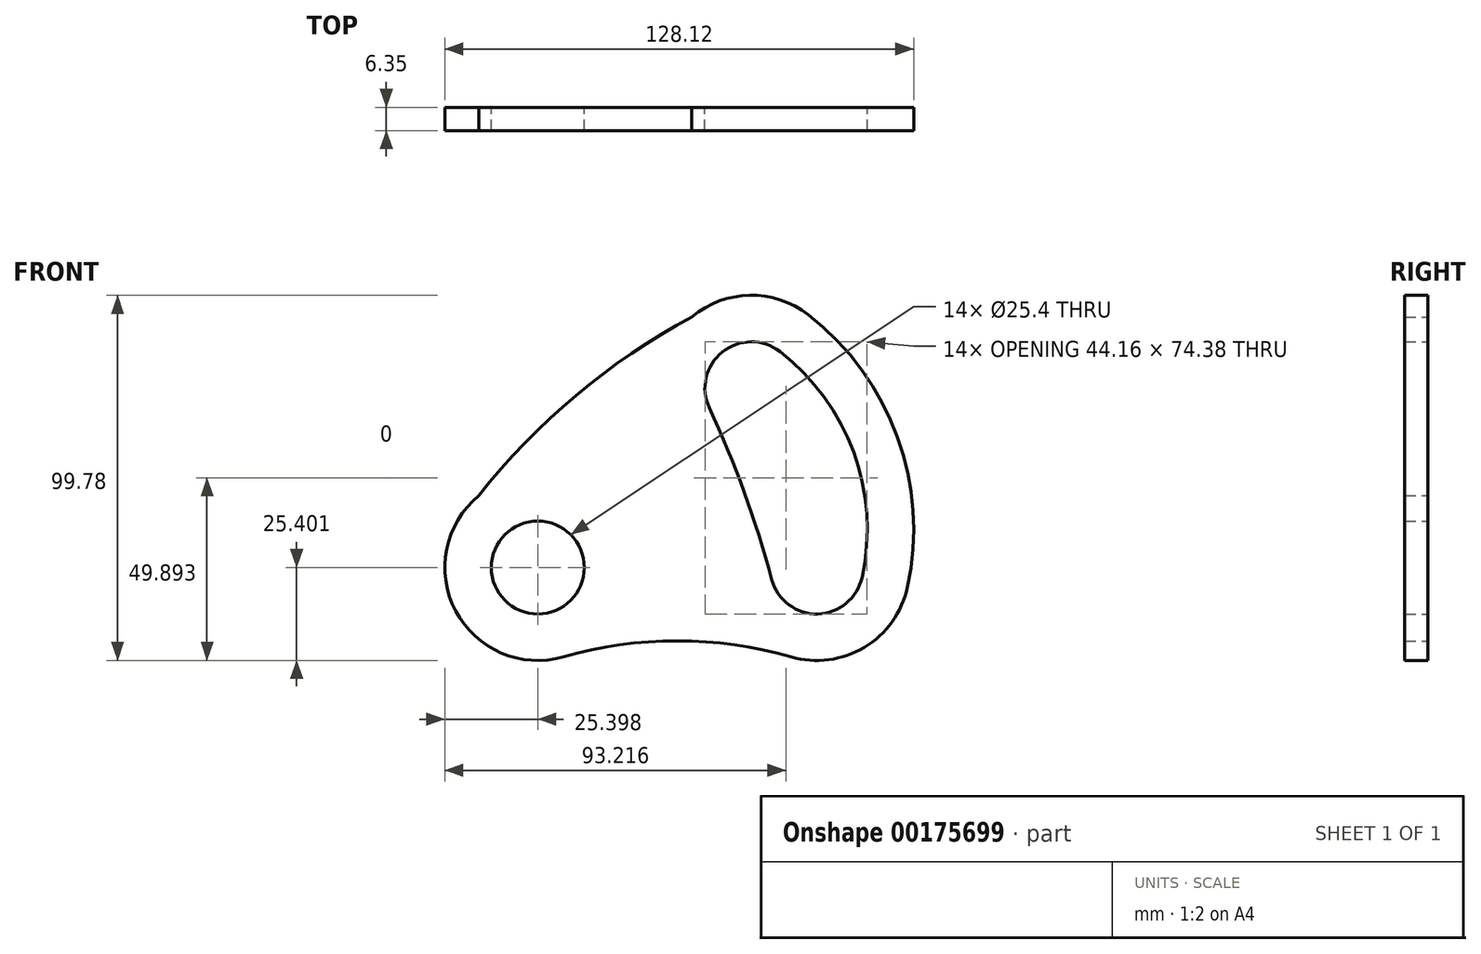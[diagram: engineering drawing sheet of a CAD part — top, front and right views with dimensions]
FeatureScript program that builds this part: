
annotation { "Feature Type Name" : "Feature", "Feature Type Description" : "" }
export const myFeature = defineFeature(function(context is Context, id is Id, definition is map)
    precondition{}
    {
        {
            var Q0;
            Q0=qCreatedBy(makeId("Front.planeOp"),FACE);
            var sketch = newSketch(context, id + "F0", { "sketchPlane" : qUnion([Q0])});
            skCircle(sketch, "E0", {"center": v(-42.07, 4.01) * mm, "radius": 25.4 * mm});
            skCircle(sketch, "E1", {"center": v(-42.07, 4.01) * mm, "radius": 12.7 * mm});
            skCircle(sketch, "E2", {"center": v(16.3, 53) * mm, "radius": 12.7 * mm});
            skCircle(sketch, "E3", {"center": v(34.13, 4.01) * mm, "radius": 12.7 * mm});
            skLineSegment(sketch, "E4", {"start": v(-42.07, 4.01) * mm, "end": v(34.13, 4.01) * mm});
            skLineSegment(sketch, "E5", {"start": v(-42.07, 4.01) * mm, "end": v(16.3, 53) * mm});
            skArc(sketch, "E6", {"start": v(21.86, 0.72) * mm, "mid": v(14.35, 24.55) * mm, "end": v(4.79, 47.63) * mm});
            skArc(sketch, "E7", {"start": v(46.53, 1.29) * mm, "mid": v(44.26, 35.43) * mm, "end": v(24.05, 63.05) * mm});
            skCircle(sketch, "E8", {"center": v(16.3, 53) * mm, "radius": 25.4 * mm});
            skCircle(sketch, "E9", {"center": v(34.13, 4.01) * mm, "radius": 25.4 * mm});
            skArc(sketch, "E10", {"start": v(58.95, -1.4) * mm, "mid": v(56.18, 39.77) * mm, "end": v(31.83, 73.09) * mm});
            skArc(sketch, "E11", {"start": v(8.74, 4.9) * mm, "mid": v(6.11, 21.55) * mm, "end": v(-2.57, 35.99) * mm});
            skArc(sketch, "E12", {"start": v(0, 72.47) * mm, "mid": v(-31.62, 51.02) * mm, "end": v(-58.23, 23.6) * mm});
            skArc(sketch, "E13", {"start": v(27.13, -20.4) * mm, "mid": v(-3.97, -16.04) * mm, "end": v(-35.07, -20.4) * mm});
            skSolve(sketch);
        }
        {
            var Q0;
            {var subQ0=sQuery(id+"F0.wireOp",EDGE,"E12");Q0=makeQuery(id+"F0.imprint","IMPRINT",FACE,{"disambiguationData":[TD([[makeQuery(id+"F0.imprint","IMPRINT",EDGE,{"derivedFrom":subQ0}),1.0]])]});}
            var Q1;
            {var subQ9=sQuery(id+"F0.wireOp",EDGE,"E11");Q1=makeQuery(id+"F0.imprint","IMPRINT",FACE,{"disambiguationData":[TD([[makeQuery(id+"F0.imprint","IMPRINT",EDGE,{"derivedFrom":subQ9}),1.0]])]});}
            var Q2;
            {var subQ0=sQuery(id+"F0.wireOp",EDGE,"E13");Q2=makeQuery(id+"F0.imprint","IMPRINT",FACE,{"disambiguationData":[TD([[makeQuery(id+"F0.imprint","IMPRINT",EDGE,{"derivedFrom":subQ0}),-1.0]])]});}
            var Q3;
            {var subQ5=sQuery(id+"F0.wireOp",EDGE,"E10");Q3=makeQuery(id+"F0.imprint","IMPRINT",FACE,{"disambiguationData":[TD([[makeQuery(id+"F0.imprint","IMPRINT",EDGE,{"derivedFrom":subQ5}),1.0]])]});}
            var Q4;
            {var subQ1=sQuery(id+"F0.wireOp",EDGE,"E2");var subQ5=sQuery(id+"F0.wireOp",EDGE,"E6");var subQ6=makeQuery(id+"F0.imprint","INTERSECT",VERTEX,{"derivedFrom":[subQ1,subQ5]});Q4=makeQuery(id+"F0.imprint","IMPRINT",FACE,{"disambiguationData":[TD([[makeQuery(id+"F0.imprint","IMPRINT",EDGE,{"disambiguationData":[TD([[subQ6,1.0]])],"derivedFrom":subQ1}),-1.0]])]});}
            var Q5;
            {var subQ0=sQuery(id+"F0.wireOp",EDGE,"E6");var subQ1=sQuery(id+"F0.wireOp",EDGE,"E3");var subQ2=makeQuery(id+"F0.imprint","INTERSECT",VERTEX,{"derivedFrom":[subQ1,subQ0]});Q5=makeQuery(id+"F0.imprint","IMPRINT",FACE,{"disambiguationData":[TD([[makeQuery(id+"F0.imprint","IMPRINT",EDGE,{"disambiguationData":[TD([[subQ2,-1.0]])],"derivedFrom":subQ1}),-1.0]])]});}
            var Q6;
            {var subQ0=sQuery(id+"F0.wireOp",EDGE,"E9");var subQ1=sQuery(id+"F0.wireOp",EDGE,"E4");var subQ2=makeQuery(id+"F0.imprint","INTERSECT",VERTEX,{"derivedFrom":[subQ1,subQ0]});Q6=makeQuery(id+"F0.imprint","IMPRINT",FACE,{"disambiguationData":[TD([[makeQuery(id+"F0.imprint","IMPRINT",EDGE,{"disambiguationData":[TD([[subQ2,-1.0]])],"derivedFrom":subQ1}),1.0]])]});}
            var Q7;
            {var subQ0=sQuery(id+"F0.wireOp",EDGE,"E8");var subQ1=sQuery(id+"F0.wireOp",EDGE,"E5");var subQ2=makeQuery(id+"F0.imprint","INTERSECT",VERTEX,{"derivedFrom":[subQ1,subQ0]});Q7=makeQuery(id+"F0.imprint","IMPRINT",FACE,{"disambiguationData":[TD([[makeQuery(id+"F0.imprint","IMPRINT",EDGE,{"disambiguationData":[TD([[subQ2,-1.0]])],"derivedFrom":subQ1}),-1.0]])]});}
            var Q8;
            {var subQ5=sQuery(id+"F0.wireOp",EDGE,"E11");Q8=makeQuery(id+"F0.imprint","IMPRINT",FACE,{"disambiguationData":[TD([[makeQuery(id+"F0.imprint","IMPRINT",EDGE,{"derivedFrom":subQ5}),-1.0]])]});}
            var Q9;
            {var subQ5=sQuery(id+"F0.wireOp",EDGE,"E0");var subQ8=makeQuery(id+"F0.imprint","INTERSECT",VERTEX,{"derivedFrom":[subQ5,sQuery(id+"F0.wireOp",EDGE,"E12")]});Q9=makeQuery(id+"F0.imprint","IMPRINT",FACE,{"disambiguationData":[TD([[makeQuery(id+"F0.imprint","IMPRINT",EDGE,{"disambiguationData":[TD([[subQ8,1.0]])],"derivedFrom":subQ5}),1.0]])]});}
            var Q10;
            {var subQ0=sQuery(id+"F0.wireOp",EDGE,"E5");var subQ1=sQuery(id+"F0.wireOp",EDGE,"E0");var subQ2=makeQuery(id+"F0.imprint","INTERSECT",VERTEX,{"derivedFrom":[subQ1,subQ0]});Q10=makeQuery(id+"F0.imprint","IMPRINT",FACE,{"disambiguationData":[TD([[makeQuery(id+"F0.imprint","IMPRINT",EDGE,{"disambiguationData":[TD([[subQ2,1.0]])],"derivedFrom":subQ1}),1.0]])]});}
            extrude(context, id + "F1", {"entities" : qUnion([Q0, Q1, Q2, Q3, Q4, Q5, Q6, Q7, Q8, Q9, Q10]), "depth" : 6.35 * mm});
        }
    });
